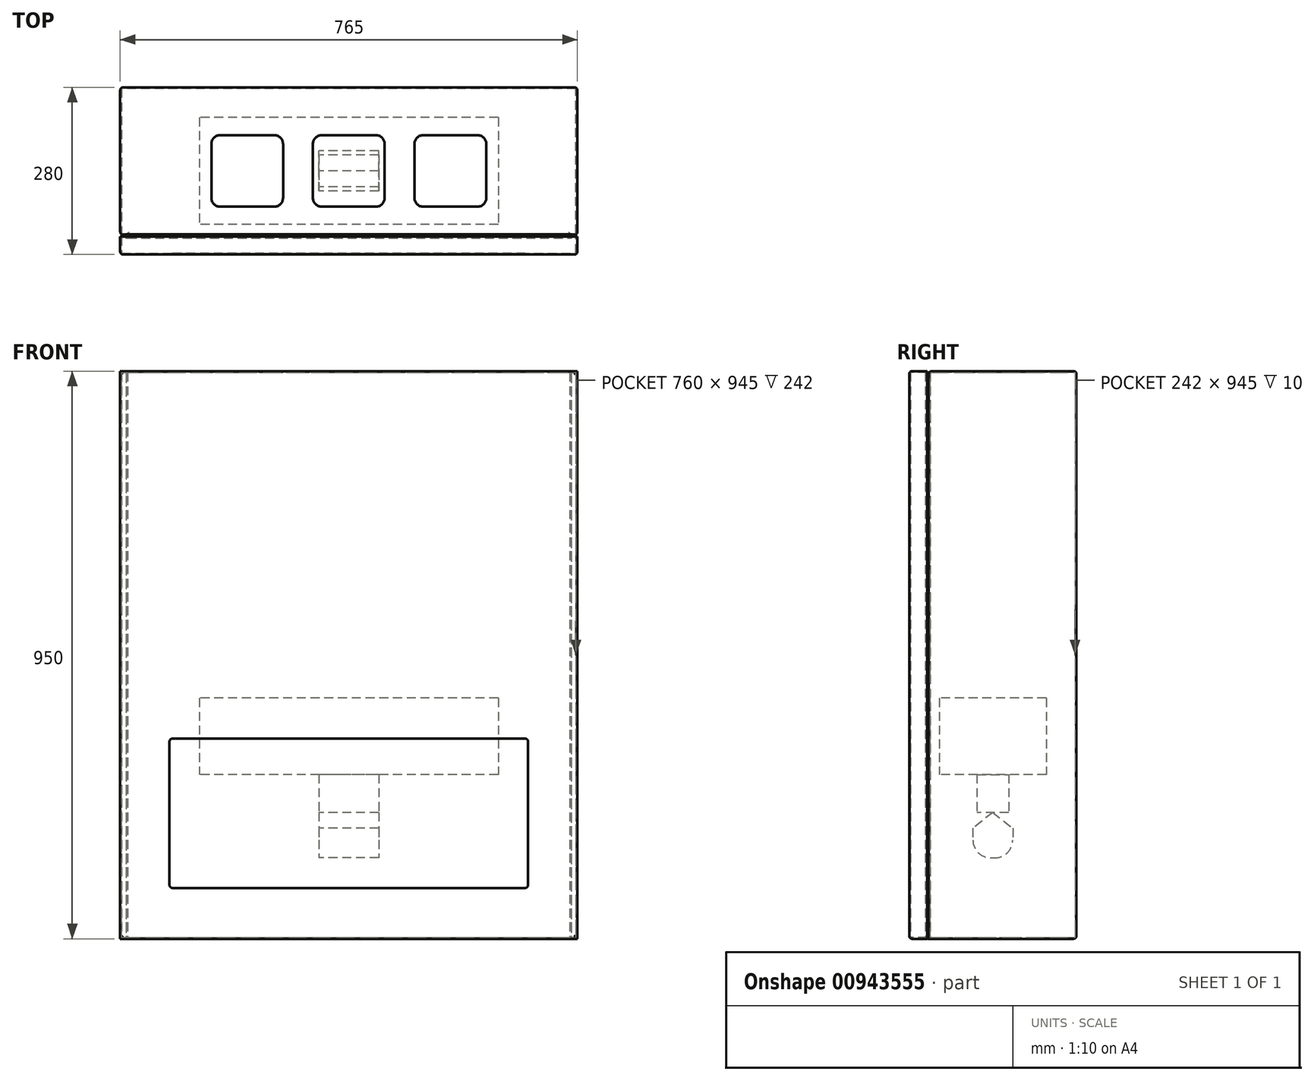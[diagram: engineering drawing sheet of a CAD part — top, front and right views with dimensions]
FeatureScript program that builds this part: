
annotation { "Feature Type Name" : "Feature", "Feature Type Description" : "" }
export const myFeature = defineFeature(function(context is Context, id is Id, definition is map)
    precondition{}
    {
        {
            var Q0;
            Q0=qCreatedBy(makeId("Front.planeOp"),FACE);
            var sketch = newSketch(context, id + "F0", { "sketchPlane" : qUnion([Q0])});
            skLineSegment(sketch, "E0", {"start": v(0, 950) * mm, "end": v(0, 0) * mm, "construction": true});
            skLineSegment(sketch, "E1", {"start": v(0, 0) * mm, "end": v(382.5, 0) * mm, "construction": true});
            skLineSegment(sketch, "E2.bottom", {"start": v(382.5, 0) * mm, "end": v(-382.5, 0) * mm});
            skLineSegment(sketch, "E2.top", {"start": v(382.5, 950) * mm, "end": v(-382.5, 950) * mm});
            skLineSegment(sketch, "E2.left", {"start": v(382.5, 0) * mm, "end": v(382.5, 950) * mm});
            skLineSegment(sketch, "E2.right", {"start": v(-382.5, 0) * mm, "end": v(-382.5, 950) * mm});
            skLineSegment(sketch, "E3.bottom", {"start": v(295, 85) * mm, "end": v(-295, 85) * mm});
            skLineSegment(sketch, "E3.top", {"start": v(295, 335) * mm, "end": v(-295, 335) * mm});
            skLineSegment(sketch, "E3.left", {"start": v(300, 90) * mm, "end": v(300, 330) * mm});
            skLineSegment(sketch, "E3.right", {"start": v(-300, 90) * mm, "end": v(-300, 330) * mm});
            skPoint(sketch, "E3.middle", {"position": v(0, 210) * mm});
            skPoint(sketch, "E4.visualSharp", {"position": v(-300, 335) * mm});
            skArc(sketch, "E4.filletArc", {"start": v(-295, 335) * mm, "mid": v(-298.54, 333.54) * mm, "end": v(-300, 330) * mm});
            skPoint(sketch, "E5.visualSharp", {"position": v(-300, 85) * mm});
            skArc(sketch, "E5.filletArc", {"start": v(-300, 90) * mm, "mid": v(-298.54, 86.46) * mm, "end": v(-295, 85) * mm});
            skPoint(sketch, "E6.visualSharp", {"position": v(300, 335) * mm});
            skArc(sketch, "E6.filletArc", {"start": v(300, 330) * mm, "mid": v(298.54, 333.54) * mm, "end": v(295, 335) * mm});
            skPoint(sketch, "E7.visualSharp", {"position": v(300, 85) * mm});
            skArc(sketch, "E7.filletArc", {"start": v(295, 85) * mm, "mid": v(298.54, 86.46) * mm, "end": v(300, 90) * mm});
            skSolve(sketch);
        }
        {
            var Q0;
            Q0=qCreatedBy(makeId("Right.planeOp"),FACE);
            var sketch = newSketch(context, id + "F1", { "sketchPlane" : qUnion([Q0])});
            skLineSegment(sketch, "E8.bottom", {"start": v(140, 0) * mm, "end": v(-140, 0) * mm});
            skLineSegment(sketch, "E8.top", {"start": v(140, 950) * mm, "end": v(-140, 950) * mm});
            skLineSegment(sketch, "E8.left", {"start": v(140, 0) * mm, "end": v(140, 950) * mm});
            skLineSegment(sketch, "E8.right", {"start": v(-140, 0) * mm, "end": v(-140, 950) * mm});
            skPoint(sketch, "E8.middle", {"position": v(0, 475) * mm});
            skLineSegment(sketch, "E9", {"start": v(-110, 950) * mm, "end": v(-110, 0) * mm});
            skLineSegment(sketch, "E10.0", {"start": v(-107, 950) * mm, "end": v(-107, 0) * mm});
            skSolve(sketch);
        }
        {
            var Q0;
            Q0=qCreatedBy(makeId("Top.planeOp"),FACE);
            var sketch = newSketch(context, id + "F2", { "sketchPlane" : qUnion([Q0])});
            skLineSegment(sketch, "E11.bottom", {"start": v(382.5, 140) * mm, "end": v(-382.5, 140) * mm});
            skLineSegment(sketch, "E11.top", {"start": v(382.5, -140) * mm, "end": v(-382.5, -140) * mm});
            skLineSegment(sketch, "E11.left", {"start": v(382.5, 140) * mm, "end": v(382.5, -140) * mm});
            skLineSegment(sketch, "E11.right", {"start": v(-382.5, 140) * mm, "end": v(-382.5, -140) * mm});
            skPoint(sketch, "E11.middle", {"position": v(0, 0) * mm});
            skLineSegment(sketch, "E12", {"start": v(-382.5, 0) * mm, "end": v(382.5, 0) * mm, "construction": true});
            skLineSegment(sketch, "E13", {"start": v(0, 140) * mm, "end": v(0, -140) * mm, "construction": true});
            skLineSegment(sketch, "E14.bottom", {"start": v(45, 60) * mm, "end": v(-45, 60) * mm});
            skLineSegment(sketch, "E14.top", {"start": v(45, -60) * mm, "end": v(-45, -60) * mm});
            skLineSegment(sketch, "E14.left", {"start": v(60, 45) * mm, "end": v(60, -45) * mm});
            skLineSegment(sketch, "E14.right", {"start": v(-60, 45) * mm, "end": v(-60, -45) * mm});
            skLineSegment(sketch, "E15.bottom", {"start": v(-125, 60) * mm, "end": v(-215, 60) * mm});
            skLineSegment(sketch, "E15.top", {"start": v(-125, -60) * mm, "end": v(-215, -60) * mm});
            skLineSegment(sketch, "E15.left", {"start": v(-110, 45) * mm, "end": v(-110, -45) * mm});
            skLineSegment(sketch, "E15.right", {"start": v(-230, 45) * mm, "end": v(-230, -45) * mm});
            skPoint(sketch, "E15.middle", {"position": v(-170, 0) * mm});
            skLineSegment(sketch, "E16.MirrorCS", {"start": v(125, 60) * mm, "end": v(215, 60) * mm});
            skLineSegment(sketch, "E17.MirrorCS", {"start": v(230, 45) * mm, "end": v(230, -45) * mm});
            skLineSegment(sketch, "E18.MirrorCS", {"start": v(125, -60) * mm, "end": v(215, -60) * mm});
            skPoint(sketch, "E19.MirrorP", {"position": v(170, 0) * mm});
            skLineSegment(sketch, "E20.MirrorCS", {"start": v(110, 45) * mm, "end": v(110, -45) * mm});
            skPoint(sketch, "E21.visualSharp", {"position": v(-230, 60) * mm});
            skArc(sketch, "E21.filletArc", {"start": v(-215, 60) * mm, "mid": v(-225.6, 55.6) * mm, "end": v(-230, 45) * mm});
            skPoint(sketch, "E22.visualSharp", {"position": v(-110, 60) * mm});
            skArc(sketch, "E22.filletArc", {"start": v(-110, 45) * mm, "mid": v(-114.4, 55.6) * mm, "end": v(-125, 60) * mm});
            skPoint(sketch, "E23.visualSharp", {"position": v(-110, -60) * mm});
            skArc(sketch, "E23.filletArc", {"start": v(-125, -60) * mm, "mid": v(-114.4, -55.6) * mm, "end": v(-110, -45) * mm});
            skPoint(sketch, "E24.visualSharp", {"position": v(-230, -60) * mm});
            skArc(sketch, "E24.filletArc", {"start": v(-230, -45) * mm, "mid": v(-225.6, -55.6) * mm, "end": v(-215, -60) * mm});
            skPoint(sketch, "E25.visualSharp", {"position": v(60, 60) * mm});
            skArc(sketch, "E25.filletArc", {"start": v(60, 45) * mm, "mid": v(55.6, 55.6) * mm, "end": v(45, 60) * mm});
            skPoint(sketch, "E26.visualSharp", {"position": v(-60, 60) * mm});
            skArc(sketch, "E26.filletArc", {"start": v(-45, 60) * mm, "mid": v(-55.6, 55.6) * mm, "end": v(-60, 45) * mm});
            skPoint(sketch, "E27.visualSharp", {"position": v(-60, -60) * mm});
            skArc(sketch, "E27.filletArc", {"start": v(-60, -45) * mm, "mid": v(-55.6, -55.6) * mm, "end": v(-45, -60) * mm});
            skPoint(sketch, "E28.visualSharp", {"position": v(60, -60) * mm});
            skArc(sketch, "E28.filletArc", {"start": v(45, -60) * mm, "mid": v(55.6, -55.6) * mm, "end": v(60, -45) * mm});
            skPoint(sketch, "E29.visualSharp", {"position": v(110, 60) * mm});
            skArc(sketch, "E29.filletArc", {"start": v(125, 60) * mm, "mid": v(114.4, 55.6) * mm, "end": v(110, 45) * mm});
            skPoint(sketch, "E30.visualSharp", {"position": v(110, -60) * mm});
            skArc(sketch, "E30.filletArc", {"start": v(110, -45) * mm, "mid": v(114.4, -55.6) * mm, "end": v(125, -60) * mm});
            skPoint(sketch, "E31.visualSharp", {"position": v(230, -60) * mm});
            skArc(sketch, "E31.filletArc", {"start": v(215, -60) * mm, "mid": v(225.6, -55.6) * mm, "end": v(230, -45) * mm});
            skPoint(sketch, "E32.visualSharp", {"position": v(230, 60) * mm});
            skArc(sketch, "E32.filletArc", {"start": v(230, 45) * mm, "mid": v(225.6, 55.6) * mm, "end": v(215, 60) * mm});
            skLineSegment(sketch, "E33", {"start": v(-382.5, -110) * mm, "end": v(382.5, -110) * mm});
            skLineSegment(sketch, "E34", {"start": v(382.5, -107) * mm, "end": v(-382.5, -107) * mm});
            skLineSegment(sketch, "E35.bottom", {"start": v(372.5, -107) * mm, "end": v(-372.5, -107) * mm});
            skLineSegment(sketch, "E35.top", {"start": v(372.5, -113) * mm, "end": v(-372.5, -113) * mm});
            skLineSegment(sketch, "E35.left", {"start": v(372.5, -107) * mm, "end": v(372.5, -113) * mm});
            skLineSegment(sketch, "E35.right", {"start": v(-372.5, -107) * mm, "end": v(-372.5, -113) * mm});
            skPoint(sketch, "E35.middle", {"position": v(0, -110) * mm});
            skSolve(sketch);
        }
        {
            var Q0;
            Q0=qCreatedBy(makeId("Top.planeOp"),FACE);
            var sketch = newSketch(context, id + "F3", { "sketchPlane" : qUnion([Q0])});
            skLineSegment(sketch, "E36.0", {"start": v(372.5, -113) * mm, "end": v(-372.5, -113) * mm});
            skPoint(sketch, "E37.0", {"position": v(372.5, -110) * mm});
            skLineSegment(sketch, "E38.0", {"start": v(372.5, -107) * mm, "end": v(372.5, -113) * mm});
            skLineSegment(sketch, "E39.0.0", {"start": v(-372.5, -107) * mm, "end": v(372.5, -107) * mm});
            skLineSegment(sketch, "E39.0.1", {"start": v(372.5, -107) * mm, "end": v(382.5, -107) * mm});
            skLineSegment(sketch, "E39.0.2", {"start": v(382.5, -107) * mm, "end": v(382.5, 140) * mm});
            skLineSegment(sketch, "E39.0.3", {"start": v(382.5, 140) * mm, "end": v(-382.5, 140) * mm});
            skLineSegment(sketch, "E39.0.4", {"start": v(-382.5, 140) * mm, "end": v(-382.5, -107) * mm});
            skLineSegment(sketch, "E39.0.5", {"start": v(-382.5, -107) * mm, "end": v(-372.5, -107) * mm});
            skPoint(sketch, "E40.0", {"position": v(-372.5, -107) * mm});
            skLineSegment(sketch, "E41.0", {"start": v(-372.5, -107) * mm, "end": v(-372.5, -113) * mm});
            skSolve(sketch);
        }
        {
            var Q0;
            Q0 = qSketchRegion(id + "F3", true);
            var Q1;
            Q1=sQuery(id+"F0.wireOp",VERTEX,"E2.top.end");
            extrude(context, id + "F4", {"entities" : qUnion([Q0]), "endBound" : BoundingType.UP_TO_VERTEX, "depth" : 25 * mm, "endBoundEntityVertex" : qUnion([Q1]), "offsetDistance" : 25 * mm});
        }
        {
            var Q0;
            Q0=makeQuery(id+"F4.opExtrude","CAP_FACE",FACE,{"disambiguationData":[OSD([sQuery(id+"F3.wireOp",EDGE,"E36.0"),sQuery(id+"F3.wireOp",EDGE,"E38.0"),sQuery(id+"F3.wireOp",EDGE,"E39.0.1"),sQuery(id+"F3.wireOp",EDGE,"E39.0.2"),sQuery(id+"F3.wireOp",EDGE,"E39.0.3"),sQuery(id+"F3.wireOp",EDGE,"E39.0.4"),sQuery(id+"F3.wireOp",EDGE,"E39.0.5"),sQuery(id+"F3.wireOp",EDGE,"E41.0")])],"isStart":false});
            var sketch = newSketch(context, id + "F5", { "sketchPlane" : qUnion([Q0])});
            skLineSegment(sketch, "E42.0", {"start": v(-125, 60) * mm, "end": v(-215, 60) * mm});
            skPoint(sketch, "E43.0", {"position": v(-225.6, 55.6) * mm});
            skLineSegment(sketch, "E44.0", {"start": v(-230, 45) * mm, "end": v(-230, -45) * mm});
            skLineSegment(sketch, "E45.0", {"start": v(-125, -60) * mm, "end": v(-215, -60) * mm});
            skArc(sketch, "E46.0", {"start": v(-230, -45) * mm, "mid": v(-225.6, -55.6) * mm, "end": v(-215, -60) * mm});
            skArc(sketch, "E47.0", {"start": v(-215, 60) * mm, "mid": v(-225.6, 55.6) * mm, "end": v(-230, 45) * mm});
            skArc(sketch, "E48.0", {"start": v(-110, 45) * mm, "mid": v(-114.4, 55.6) * mm, "end": v(-125, 60) * mm});
            skLineSegment(sketch, "E49.0", {"start": v(-110, 45) * mm, "end": v(-110, -45) * mm});
            skArc(sketch, "E50.0", {"start": v(-125, -60) * mm, "mid": v(-114.4, -55.6) * mm, "end": v(-110, -45) * mm});
            skArc(sketch, "E51.0", {"start": v(-60, -45) * mm, "mid": v(-55.6, -55.6) * mm, "end": v(-45, -60) * mm});
            skLineSegment(sketch, "E52.0", {"start": v(-60, 45) * mm, "end": v(-60, -45) * mm});
            skArc(sketch, "E53.0", {"start": v(-45, 60) * mm, "mid": v(-55.6, 55.6) * mm, "end": v(-60, 45) * mm});
            skLineSegment(sketch, "E54.0", {"start": v(45, 60) * mm, "end": v(-45, 60) * mm});
            skPoint(sketch, "E55.0", {"position": v(55.6, 55.6) * mm});
            skArc(sketch, "E56.0", {"start": v(60, 45) * mm, "mid": v(55.6, 55.6) * mm, "end": v(45, 60) * mm});
            skLineSegment(sketch, "E57.0", {"start": v(60, 45) * mm, "end": v(60, -45) * mm});
            skArc(sketch, "E58.0", {"start": v(45, -60) * mm, "mid": v(55.6, -55.6) * mm, "end": v(60, -45) * mm});
            skLineSegment(sketch, "E59.0", {"start": v(45, -60) * mm, "end": v(-45, -60) * mm});
            skArc(sketch, "E60.0", {"start": v(230, 45) * mm, "mid": v(225.6, 55.6) * mm, "end": v(215, 60) * mm});
            skLineSegment(sketch, "E61.0", {"start": v(125, 60) * mm, "end": v(215, 60) * mm});
            skLineSegment(sketch, "E62.0", {"start": v(230, 45) * mm, "end": v(230, -45) * mm});
            skArc(sketch, "E63.0", {"start": v(215, -60) * mm, "mid": v(225.6, -55.6) * mm, "end": v(230, -45) * mm});
            skLineSegment(sketch, "E64.0", {"start": v(125, -60) * mm, "end": v(215, -60) * mm});
            skArc(sketch, "E65.0", {"start": v(110, -45) * mm, "mid": v(114.4, -55.6) * mm, "end": v(125, -60) * mm});
            skLineSegment(sketch, "E66.0", {"start": v(110, 45) * mm, "end": v(110, -45) * mm});
            skArc(sketch, "E67.0", {"start": v(125, 60) * mm, "mid": v(114.4, 55.6) * mm, "end": v(110, 45) * mm});
            skLineSegment(sketch, "E68.0", {"start": v(372.5, -107) * mm, "end": v(-372.5, -107) * mm});
            skLineSegment(sketch, "E69.0", {"start": v(-372.5, -107) * mm, "end": v(-372.5, -113) * mm});
            skLineSegment(sketch, "E70.0", {"start": v(372.5, -113) * mm, "end": v(-372.5, -113) * mm});
            skLineSegment(sketch, "E71.0", {"start": v(372.5, -107) * mm, "end": v(372.5, -113) * mm});
            skSolve(sketch);
        }
        {
            var Q0;
            Q0=makeQuery(id+"F4.opExtrude","SWEPT_FACE",FACE,{"disambiguationData":[OSD([sQuery(id+"F3.wireOp",EDGE,"E36.0")])]});
            shell(context, id + "F6", {"entities" : qUnion([Q0]), "thickness" : 2.5 * mm});
        }
        {
            var Q0;
            Q0 = qSketchRegion(id + "F5", true);
            var Q1;
            {var subQ0=sQuery(id+"F3.wireOp",EDGE,"E41.0");var subQ1=sQuery(id+"F3.wireOp",EDGE,"E39.0.5");var subQ2=sQuery(id+"F3.wireOp",EDGE,"E39.0.4");var subQ3=sQuery(id+"F3.wireOp",EDGE,"E39.0.3");var subQ4=sQuery(id+"F3.wireOp",EDGE,"E39.0.2");var subQ5=sQuery(id+"F3.wireOp",EDGE,"E39.0.1");var subQ6=sQuery(id+"F3.wireOp",EDGE,"E38.0");var subQ7=sQuery(id+"F3.wireOp",EDGE,"E36.0");Q1=makeQuery(id+"F6.opShell","OFFSET_FACE",FACE,{"disambiguationData":[OSD([subQ7,subQ6,subQ5,subQ4,subQ3,subQ2,subQ1,subQ0]),TDD([makeQuery(id+"F4.opExtrude","CAP_FACE",FACE,{"disambiguationData":[OSD([subQ7,subQ6,subQ5,subQ4,subQ3,subQ2,subQ1,subQ0])],"isStart":false})])]});}
            extrude(context, id + "F7", {"entities" : qUnion([Q0]), "operationType" : NewBodyOperationType.REMOVE, "endBound" : BoundingType.UP_TO_SURFACE, "oppositeDirection" : true, "depth" : 5 * mm, "endBoundEntityFace" : qUnion([Q1]), "offsetDistance" : 25 * mm});
        }
        {
            var Q0;
            Q0=qCreatedBy(makeId("Top.planeOp"),FACE);
            var sketch = newSketch(context, id + "F8", { "sketchPlane" : qUnion([Q0])});
            skLineSegment(sketch, "E72.0.0", {"start": v(-372.5, -110) * mm, "end": v(-382.5, -110) * mm});
            skLineSegment(sketch, "E72.0.1", {"start": v(-382.5, -110) * mm, "end": v(-382.5, -140) * mm});
            skLineSegment(sketch, "E72.0.2", {"start": v(-382.5, -140) * mm, "end": v(382.5, -140) * mm});
            skLineSegment(sketch, "E72.0.3", {"start": v(382.5, -140) * mm, "end": v(382.5, -110) * mm});
            skLineSegment(sketch, "E72.0.4", {"start": v(382.5, -110) * mm, "end": v(372.5, -110) * mm});
            skLineSegment(sketch, "E73.1", {"start": v(-382.5, -110) * mm, "end": v(382.5, -110) * mm});
            skSolve(sketch);
        }
        {
            var Q0;
            Q0 = qSketchRegion(id + "F8", true);
            var Q1;
            Q1=sQuery(id+"F1.wireOp",VERTEX,"E8.top.end");
            extrude(context, id + "F9", {"entities" : qUnion([Q0]), "endBound" : BoundingType.UP_TO_VERTEX, "depth" : 25 * mm, "endBoundEntityVertex" : qUnion([Q1]), "offsetDistance" : 25 * mm});
        }
        {
            var Q0;
            Q0=makeQuery(id+"F9.opExtrude","SWEPT_FACE",FACE,{"disambiguationData":[OSD([sQuery(id+"F8.wireOp",EDGE,"E73.1")])]});
            shell(context, id + "F10", {"entities" : qUnion([Q0]), "thickness" : 2.5 * mm});
        }
        {
            var Q0;
            Q0=makeQuery(id+"F9.opExtrude","SWEPT_FACE",FACE,{"disambiguationData":[OSD([sQuery(id+"F8.wireOp",EDGE,"E72.0.2")])]});
            var sketch = newSketch(context, id + "F11", { "sketchPlane" : qUnion([Q0])});
            skLineSegment(sketch, "E74.0", {"start": v(295, 335) * mm, "end": v(-295, 335) * mm});
            skArc(sketch, "E75.0", {"start": v(-295, 335) * mm, "mid": v(-298.54, 333.54) * mm, "end": v(-300, 330) * mm});
            skLineSegment(sketch, "E76.0", {"start": v(-300, 90) * mm, "end": v(-300, 330) * mm});
            skArc(sketch, "E77.0", {"start": v(300, 330) * mm, "mid": v(298.54, 333.54) * mm, "end": v(295, 335) * mm});
            skLineSegment(sketch, "E78.0", {"start": v(300, 90) * mm, "end": v(300, 330) * mm});
            skLineSegment(sketch, "E79.0", {"start": v(295, 85) * mm, "end": v(-295, 85) * mm});
            skArc(sketch, "E80.0", {"start": v(295, 85) * mm, "mid": v(298.54, 86.46) * mm, "end": v(300, 90) * mm});
            skArc(sketch, "E81.0", {"start": v(-300, 90) * mm, "mid": v(-298.54, 86.46) * mm, "end": v(-295, 85) * mm});
            skSolve(sketch);
        }
        {
            var Q0;
            Q0 = qSketchRegion(id + "F11", true);
            var Q1;
            Q1=makeQuery(id+"F10.opShell","OFFSET_FACE",FACE,{"disambiguationData":[OSD([sQuery(id+"F8.wireOp",EDGE,"E72.0.2")])]});
            extrude(context, id + "F12", {"entities" : qUnion([Q0]), "operationType" : NewBodyOperationType.REMOVE, "endBound" : BoundingType.UP_TO_SURFACE, "oppositeDirection" : true, "depth" : 25 * mm, "endBoundEntityFace" : qUnion([Q1]), "offsetDistance" : 25 * mm});
        }
        {
            var Q0;
            Q0=qCreatedBy(makeId("Right.planeOp"),FACE);
            var sketch = newSketch(context, id + "F13", { "sketchPlane" : qUnion([Q0])});
            skLineSegment(sketch, "E82.bottom", {"start": v(89.57, 402.78) * mm, "end": v(-89.57, 402.78) * mm});
            skLineSegment(sketch, "E82.top", {"start": v(89.57, 275.02) * mm, "end": v(-89.57, 275.02) * mm});
            skLineSegment(sketch, "E82.left", {"start": v(89.57, 402.78) * mm, "end": v(89.57, 275.02) * mm});
            skLineSegment(sketch, "E82.right", {"start": v(-89.57, 402.78) * mm, "end": v(-89.57, 275.02) * mm});
            skPoint(sketch, "E82.middle", {"position": v(0, 338.9) * mm});
            skLineSegment(sketch, "E83", {"start": v(0, 402.78) * mm, "end": v(0, 0) * mm, "construction": true});
            skLineSegment(sketch, "E84.bottom", {"start": v(26.5, 275.02) * mm, "end": v(-26.5, 275.02) * mm});
            skLineSegment(sketch, "E84.top", {"start": v(26.5, 211.3) * mm, "end": v(-26.5, 211.3) * mm});
            skLineSegment(sketch, "E84.left", {"start": v(26.5, 275.02) * mm, "end": v(26.5, 211.3) * mm});
            skLineSegment(sketch, "E84.right", {"start": v(-26.5, 275.02) * mm, "end": v(-26.5, 211.3) * mm});
            skPoint(sketch, "E84.middle", {"position": v(0, 243.16) * mm});
            skLineSegment(sketch, "E85", {"start": v(0, 211.3) * mm, "end": v(-33.35, 184.89) * mm});
            skLineSegment(sketch, "E86", {"start": v(-33.35, 184.89) * mm, "end": v(-33.35, 165.46) * mm});
            skPoint(sketch, "E87.visualSharp", {"position": v(-33.35, 122.45) * mm});
            skArc(sketch, "E87.filletArc", {"start": v(-33.35, 165.46) * mm, "mid": v(-23.34, 143.1) * mm, "end": v(0, 135.65) * mm});
            skLineSegment(sketch, "E88.MirrorCS", {"start": v(0, 211.3) * mm, "end": v(33.35, 184.89) * mm});
            skLineSegment(sketch, "E89.MirrorCS", {"start": v(33.35, 184.89) * mm, "end": v(33.35, 165.46) * mm});
            skArc(sketch, "E90.MirrorCS", {"start": v(33.35, 165.46) * mm, "mid": v(23.34, 143.1) * mm, "end": v(0, 135.65) * mm});
            skSolve(sketch);
        }
        {
            var Q0;
            {var subQ1=sQuery(id+"F13.wireOp",EDGE,"E85");var subQ4=sQuery(id+"F13.wireOp",EDGE,"E84.left");Q0=qUnion([makeQuery(id+"F13.imprint","IMPRINT",FACE,{"disambiguationData":[TD([[makeQuery(id+"F13.imprint","IMPRINT",EDGE,{"derivedFrom":subQ1}),1.0]])]}),makeQuery(id+"F13.imprint","IMPRINT",FACE,{"disambiguationData":[TD([[makeQuery(id+"F13.imprint","IMPRINT",EDGE,{"derivedFrom":sQuery(id+"F13.wireOp",EDGE,"E82.bottom")}),1.0]])]}),makeQuery(id+"F13.imprint","IMPRINT",FACE,{"disambiguationData":[TD([[makeQuery(id+"F13.imprint","IMPRINT",EDGE,{"derivedFrom":subQ4}),-1.0]])]})]);}
            extrude(context, id + "F14", {"entities" : qUnion([Q0]), "depth" : 50 * mm, "offsetDistance" : 25 * mm, "hasSecondDirection" : true, "secondDirectionOppositeDirection" : true, "secondDirectionDepth" : 50 * mm});
        }
        {
            var Q0;
            Q0=makeQuery(id+"F13.imprint","IMPRINT",FACE,{"disambiguationData":[TD([[makeQuery(id+"F13.imprint","IMPRINT",EDGE,{"derivedFrom":sQuery(id+"F13.wireOp",EDGE,"E82.bottom")}),1.0]])]});
            extrude(context, id + "F15", {"entities" : qUnion([Q0]), "operationType" : NewBodyOperationType.ADD, "depth" : 250 * mm, "offsetDistance" : 25 * mm, "hasSecondDirection" : true, "secondDirectionOppositeDirection" : true, "secondDirectionDepth" : 250 * mm});
        }
        {
            var Q0;
            Q0=makeQuery(id+"F9.opExtrude","SWEPT_FACE",FACE,{"disambiguationData":[OSD([sQuery(id+"F8.wireOp",EDGE,"E72.0.2")])]});
            var sketch = newSketch(context, id + "F16", { "sketchPlane" : qUnion([Q0])});
            skArc(sketch, "E91.0.0", {"start": v(300, 330) * mm, "mid": v(298.54, 333.54) * mm, "end": v(295, 335) * mm});
            skLineSegment(sketch, "E91.0.1", {"start": v(295, 335) * mm, "end": v(-295, 335) * mm});
            skArc(sketch, "E91.0.2", {"start": v(-295, 335) * mm, "mid": v(-298.54, 333.54) * mm, "end": v(-300, 330) * mm});
            skLineSegment(sketch, "E91.0.3", {"start": v(-300, 330) * mm, "end": v(-300, 90) * mm});
            skArc(sketch, "E91.0.4", {"start": v(-300, 90) * mm, "mid": v(-298.54, 86.46) * mm, "end": v(-295, 85) * mm});
            skLineSegment(sketch, "E91.0.5", {"start": v(-295, 85) * mm, "end": v(295, 85) * mm});
            skArc(sketch, "E91.0.6", {"start": v(295, 85) * mm, "mid": v(298.54, 86.46) * mm, "end": v(300, 90) * mm});
            skLineSegment(sketch, "E91.0.7", {"start": v(300, 90) * mm, "end": v(300, 330) * mm});
            skSolve(sketch);
        }
        {
            var Q0;
            Q0 = qSketchRegion(id + "F16", true);
            var Q1;
            Q1=makeQuery(id+"F10.opShell","OFFSET_FACE",FACE,{"disambiguationData":[OSD([sQuery(id+"F8.wireOp",EDGE,"E72.0.2")])]});
            extrude(context, id + "F17", {"entities" : qUnion([Q0]), "endBound" : BoundingType.UP_TO_SURFACE, "oppositeDirection" : true, "depth" : 25 * mm, "endBoundEntityFace" : qUnion([Q1]), "offsetDistance" : 25 * mm});
        }
        {
            var Q0;
            Q0=makeQuery(id+"F9.opExtrude","SWEPT_EDGE",EDGE,{"disambiguationData":[OSD([sQuery(id+"F8.wireOp",EDGE,"E72.0.1"),sQuery(id+"F8.wireOp",EDGE,"E72.0.2")])]});
            var Q1;
            Q1=makeQuery(id+"F9.opExtrude","CAP_EDGE",EDGE,{"disambiguationData":[OSD([sQuery(id+"F8.wireOp",EDGE,"E72.0.2")])],"isStart":false});
            var Q2;
            Q2=makeQuery(id+"F9.opExtrude","SWEPT_FACE",FACE,{"disambiguationData":[OSD([sQuery(id+"F8.wireOp",EDGE,"E72.0.2")])]});
            var Q3;
            Q3=makeQuery(id+"F4.opExtrude","SWEPT_FACE",FACE,{"disambiguationData":[OSD([sQuery(id+"F3.wireOp",EDGE,"E39.0.2")])]});
            var Q4;
            Q4=makeQuery(id+"F4.opExtrude","CAP_FACE",FACE,{"disambiguationData":[OSD([sQuery(id+"F3.wireOp",EDGE,"E36.0"),sQuery(id+"F3.wireOp",EDGE,"E38.0"),sQuery(id+"F3.wireOp",EDGE,"E39.0.1"),sQuery(id+"F3.wireOp",EDGE,"E39.0.2"),sQuery(id+"F3.wireOp",EDGE,"E39.0.3"),sQuery(id+"F3.wireOp",EDGE,"E39.0.4"),sQuery(id+"F3.wireOp",EDGE,"E39.0.5"),sQuery(id+"F3.wireOp",EDGE,"E41.0")])],"isStart":false});
            var Q5;
            Q5=makeQuery(id+"F4.opExtrude","SWEPT_FACE",FACE,{"disambiguationData":[OSD([sQuery(id+"F3.wireOp",EDGE,"E39.0.3")])]});
            var Q6;
            Q6=makeQuery(id+"F4.opExtrude","SWEPT_FACE",FACE,{"disambiguationData":[OSD([sQuery(id+"F3.wireOp",EDGE,"E39.0.4")])]});
            var Q7;
            Q7=makeQuery(id+"F4.opExtrude","CAP_FACE",FACE,{"disambiguationData":[OSD([sQuery(id+"F3.wireOp",EDGE,"E36.0"),sQuery(id+"F3.wireOp",EDGE,"E38.0"),sQuery(id+"F3.wireOp",EDGE,"E39.0.1"),sQuery(id+"F3.wireOp",EDGE,"E39.0.2"),sQuery(id+"F3.wireOp",EDGE,"E39.0.3"),sQuery(id+"F3.wireOp",EDGE,"E39.0.4"),sQuery(id+"F3.wireOp",EDGE,"E39.0.5"),sQuery(id+"F3.wireOp",EDGE,"E41.0")])],"isStart":true});
            fillet(context, id + "F18", {"entities" : qUnion([Q0, Q1, Q2, Q3, Q4, Q5, Q6, Q7]), "radius" : 5 * mm, "tangentPropagation" : true, "allowEdgeOverflow" : false});
        }
    });
